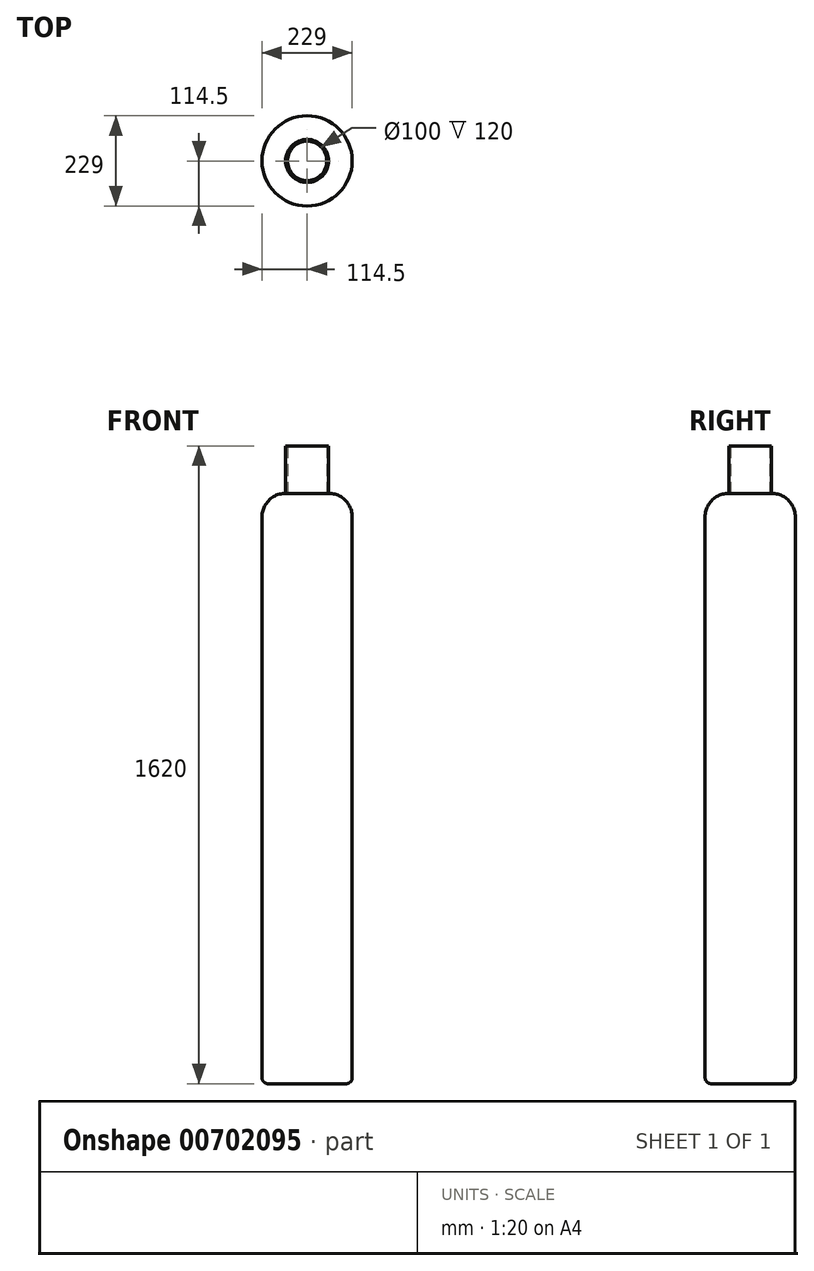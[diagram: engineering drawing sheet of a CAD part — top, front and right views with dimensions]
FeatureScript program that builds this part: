
annotation { "Feature Type Name" : "Feature", "Feature Type Description" : "" }
export const myFeature = defineFeature(function(context is Context, id is Id, definition is map)
    precondition{}
    {
        {
            var Q0;
            Q0=qCreatedBy(makeId("Top.planeOp"),FACE);
            var sketch = newSketch(context, id + "F0", { "sketchPlane" : qUnion([Q0])});
            skCircle(sketch, "E0", {"center": v(0, 0) * mm, "radius": 114.5 * mm});
            skSolve(sketch);
        }
        {
            var Q0;
            Q0=makeQuery(id+"F0.imprint","IMPRINT",FACE,{"disambiguationData":[TD([[makeQuery(id+"F0.imprint","IMPRINT",EDGE,{"derivedFrom":sQuery(id+"F0.wireOp",EDGE,"E0")}),1.0]])]});
            extrude(context, id + "F1", {"entities" : qUnion([Q0]), "depth" : 1500 * mm, "offsetDistance" : 25 * mm});
        }
        {
            var Q0;
            Q0=makeQuery(id+"F1.opExtrude","CAP_EDGE",EDGE,{"disambiguationData":[OSD([sQuery(id+"F0.wireOp",EDGE,"E0")])],"isStart":false});
            fillet(context, id + "F2", {"entities" : qUnion([Q0]), "radius" : 60 * mm, "tangentPropagation" : true, "allowEdgeOverflow" : false});
        }
        {
            var Q0;
            Q0=makeQuery(id+"F1.opExtrude","CAP_EDGE",EDGE,{"disambiguationData":[OSD([sQuery(id+"F0.wireOp",EDGE,"E0")])],"isStart":true});
            fillet(context, id + "F3", {"entities" : qUnion([Q0]), "radius" : 15 * mm, "tangentPropagation" : true, "allowEdgeOverflow" : false});
        }
        {
            var Q0;
            Q0=makeQuery(id+"F1.opExtrude","CAP_FACE",FACE,{"disambiguationData":[OSD([sQuery(id+"F0.wireOp",EDGE,"E0")])],"isStart":false});
            var sketch = newSketch(context, id + "F4", { "sketchPlane" : qUnion([Q0])});
            skCircle(sketch, "E1", {"center": v(0, 0) * mm, "radius": 55 * mm});
            skCircle(sketch, "E2", {"center": v(0, 0) * mm, "radius": 50 * mm});
            skSolve(sketch);
        }
        {
            var Q0;
            Q0=makeQuery(id+"F4.imprint","IMPRINT",FACE,{"disambiguationData":[TD([[makeQuery(id+"F4.imprint","IMPRINT",EDGE,{"derivedFrom":sQuery(id+"F4.wireOp",EDGE,"E2")}),-1.0]])]});
            extrude(context, id + "F5", {"entities" : qUnion([Q0]), "operationType" : NewBodyOperationType.ADD, "depth" : 120 * mm, "offsetDistance" : 25 * mm});
        }
    });
